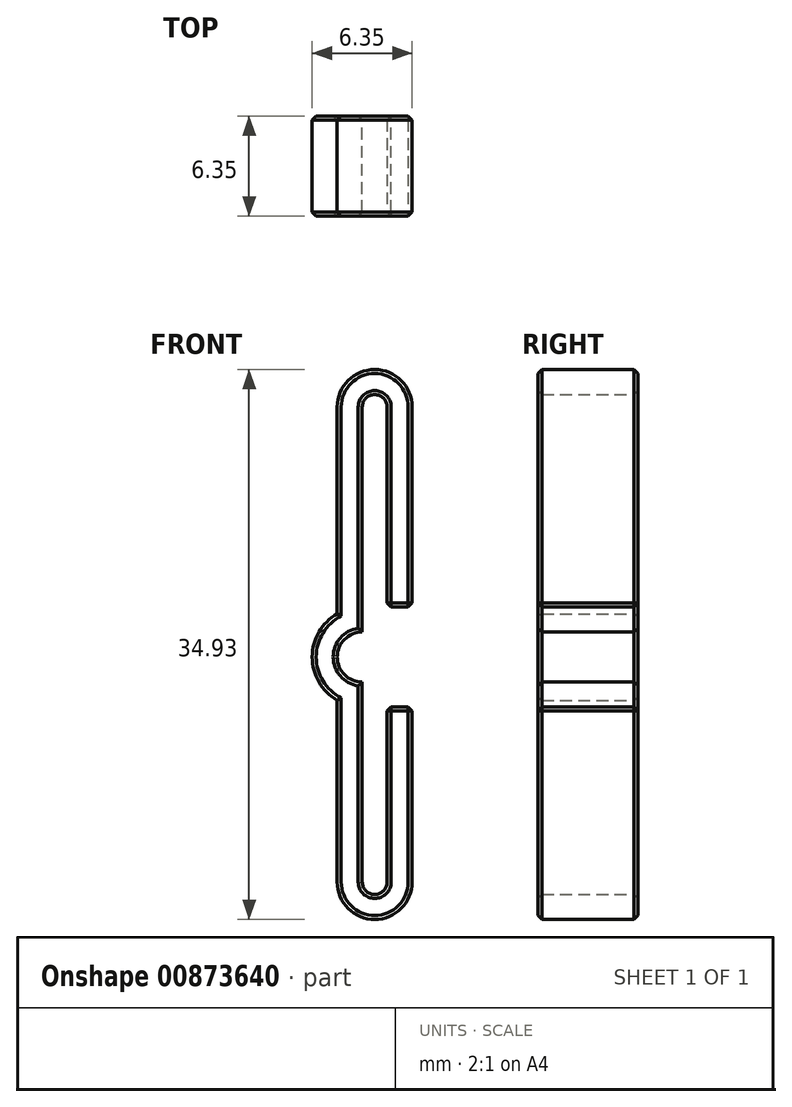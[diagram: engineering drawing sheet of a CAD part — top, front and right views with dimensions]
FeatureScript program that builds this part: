
annotation { "Feature Type Name" : "Feature", "Feature Type Description" : "" }
export const myFeature = defineFeature(function(context is Context, id is Id, definition is map)
    precondition{}
    {
        {
            var Q0;
            Q0=qCreatedBy(makeId("Front.planeOp"),FACE);
            var sketch = newSketch(context, id + "F0", { "sketchPlane" : qUnion([Q0])});
            skLineSegment(sketch, "E0", {"start": v(0, 15.88) * mm, "end": v(0, 1.59) * mm});
            skLineSegment(sketch, "E1", {"start": v(1.59, 15.88) * mm, "end": v(1.59, 3.18) * mm});
            skLineSegment(sketch, "E2", {"start": v(-1.59, 15.88) * mm, "end": v(-1.59, 2.75) * mm});
            skLineSegment(sketch, "E3", {"start": v(3.17, 15.88) * mm, "end": v(3.17, 3.18) * mm});
            skArc(sketch, "E4", {"start": v(3.17, 15.88) * mm, "mid": v(0.8, 18.26) * mm, "end": v(-1.59, 15.88) * mm});
            skArc(sketch, "E5", {"start": v(-1.59, -14.29) * mm, "mid": v(0.8, -16.67) * mm, "end": v(3.18, -14.29) * mm});
            skArc(sketch, "E6", {"start": v(0, -14.29) * mm, "mid": v(0.8, -15.08) * mm, "end": v(1.59, -14.29) * mm});
            skArc(sketch, "E7", {"start": v(1.59, 15.88) * mm, "mid": v(0.8, 16.67) * mm, "end": v(0, 15.88) * mm});
            skArc(sketch, "E8", {"start": v(0, -1.59) * mm, "mid": v(-1.59, 0) * mm, "end": v(0, 1.59) * mm});
            skArc(sketch, "E9", {"start": v(-1.59, 2.75) * mm, "mid": v(-3.18, 0) * mm, "end": v(-1.59, -2.75) * mm});
            skLineSegment(sketch, "E10.trimOffspring", {"start": v(-1.59, -2.75) * mm, "end": v(-1.59, -14.29) * mm});
            skLineSegment(sketch, "E11", {"start": v(1.59, 3.18) * mm, "end": v(3.17, 3.18) * mm});
            skLineSegment(sketch, "E12.trimOffspring", {"start": v(1.59, -3.17) * mm, "end": v(1.59, -14.29) * mm});
            skLineSegment(sketch, "E13.trimOffspring", {"start": v(3.18, -3.17) * mm, "end": v(3.18, -14.29) * mm});
            skLineSegment(sketch, "E14.trimOffspring", {"start": v(0, -1.59) * mm, "end": v(0, -14.29) * mm});
            skLineSegment(sketch, "E15", {"start": v(1.59, -3.17) * mm, "end": v(3.18, -3.17) * mm});
            skSolve(sketch);
        }
        {
            var Q0;
            Q0=makeQuery(id+"F0.imprint","IMPRINT",FACE,{"disambiguationData":[TD([[makeQuery(id+"F0.imprint","IMPRINT",EDGE,{"derivedFrom":sQuery(id+"F0.wireOp",EDGE,"E0")}),-1.0]])]});
            var Q1;
            {var subQ0=sQuery(id+"F0.wireOp",EDGE,"E8");Q1=makeQuery(id+"F0.imprint","IMPRINT",FACE,{"disambiguationData":[TD([[makeQuery(id+"F0.imprint","IMPRINT",EDGE,{"derivedFrom":subQ0}),1.0]])]});}
            var Q2;
            {var subQ1=sQuery(id+"F0.wireOp",EDGE,"E5");Q2=makeQuery(id+"F0.imprint","IMPRINT",FACE,{"disambiguationData":[TD([[makeQuery(id+"F0.imprint","IMPRINT",EDGE,{"derivedFrom":subQ1}),1.0]])]});}
            extrude(context, id + "F1", {"entities" : qUnion([Q0, Q1, Q2]), "depth" : 6.35 * mm, "offsetDistance" : 25.4 * mm});
        }
        {
            var Q0;
            Q0=makeQuery(id+"F1.opExtrude","CAP_EDGE",EDGE,{"disambiguationData":[OSD([sQuery(id+"F0.wireOp",EDGE,"E2")])],"isStart":false});
            var Q1;
            Q1=makeQuery(id+"F1.opExtrude","CAP_EDGE",EDGE,{"disambiguationData":[OSD([sQuery(id+"F0.wireOp",EDGE,"E4")])],"isStart":false});
            var Q2;
            Q2=makeQuery(id+"F1.opExtrude","CAP_EDGE",EDGE,{"disambiguationData":[OSD([sQuery(id+"F0.wireOp",EDGE,"E3")])],"isStart":false});
            var Q3;
            Q3=makeQuery(id+"F1.opExtrude","CAP_EDGE",EDGE,{"disambiguationData":[OSD([sQuery(id+"F0.wireOp",EDGE,"E9")])],"isStart":false});
            var Q4;
            Q4=makeQuery(id+"F1.opExtrude","CAP_EDGE",EDGE,{"disambiguationData":[OSD([sQuery(id+"F0.wireOp",EDGE,"E10.trimOffspring")])],"isStart":false});
            var Q5;
            Q5=makeQuery(id+"F1.opExtrude","CAP_EDGE",EDGE,{"disambiguationData":[OSD([sQuery(id+"F0.wireOp",EDGE,"E5")])],"isStart":false});
            var Q6;
            Q6=makeQuery(id+"F1.opExtrude","CAP_EDGE",EDGE,{"disambiguationData":[OSD([sQuery(id+"F0.wireOp",EDGE,"E13.trimOffspring")])],"isStart":false});
            var Q7;
            Q7=makeQuery(id+"F1.opExtrude","CAP_EDGE",EDGE,{"disambiguationData":[OSD([sQuery(id+"F0.wireOp",EDGE,"E11")])],"isStart":false});
            var Q8;
            Q8=makeQuery(id+"F1.opExtrude","CAP_EDGE",EDGE,{"disambiguationData":[OSD([sQuery(id+"F0.wireOp",EDGE,"E15")])],"isStart":false});
            var Q9;
            Q9=makeQuery(id+"F1.opExtrude","CAP_EDGE",EDGE,{"disambiguationData":[OSD([sQuery(id+"F0.wireOp",EDGE,"E14.trimOffspring")])],"isStart":false});
            var Q10;
            Q10=makeQuery(id+"F1.opExtrude","CAP_EDGE",EDGE,{"disambiguationData":[OSD([sQuery(id+"F0.wireOp",EDGE,"E8")])],"isStart":false});
            var Q11;
            Q11=makeQuery(id+"F1.opExtrude","CAP_EDGE",EDGE,{"disambiguationData":[OSD([sQuery(id+"F0.wireOp",EDGE,"E0")])],"isStart":false});
            var Q12;
            Q12=makeQuery(id+"F1.opExtrude","SWEPT_EDGE",EDGE,{"disambiguationData":[OSD([sQuery(id+"F0.wireOp",EDGE,"E1"),sQuery(id+"F0.wireOp",EDGE,"E11")])]});
            var Q13;
            Q13=makeQuery(id+"F1.opExtrude","SWEPT_EDGE",EDGE,{"disambiguationData":[OSD([sQuery(id+"F0.wireOp",EDGE,"E12.trimOffspring"),sQuery(id+"F0.wireOp",EDGE,"E15")])]});
            var Q14;
            Q14=makeQuery(id+"F1.opExtrude","CAP_EDGE",EDGE,{"disambiguationData":[OSD([sQuery(id+"F0.wireOp",EDGE,"E15")])],"isStart":true});
            var Q15;
            Q15=makeQuery(id+"F1.opExtrude","SWEPT_EDGE",EDGE,{"disambiguationData":[OSD([sQuery(id+"F0.wireOp",EDGE,"E13.trimOffspring"),sQuery(id+"F0.wireOp",EDGE,"E15")])]});
            var Q16;
            Q16=makeQuery(id+"F1.opExtrude","CAP_EDGE",EDGE,{"disambiguationData":[OSD([sQuery(id+"F0.wireOp",EDGE,"E11")])],"isStart":true});
            var Q17;
            Q17=makeQuery(id+"F1.opExtrude","SWEPT_EDGE",EDGE,{"disambiguationData":[OSD([sQuery(id+"F0.wireOp",EDGE,"E3"),sQuery(id+"F0.wireOp",EDGE,"E11")])]});
            var Q18;
            Q18=makeQuery(id+"F1.opExtrude","CAP_EDGE",EDGE,{"disambiguationData":[OSD([sQuery(id+"F0.wireOp",EDGE,"E3")])],"isStart":true});
            var Q19;
            Q19=makeQuery(id+"F1.opExtrude","CAP_EDGE",EDGE,{"disambiguationData":[OSD([sQuery(id+"F0.wireOp",EDGE,"E13.trimOffspring")])],"isStart":true});
            var Q20;
            Q20=makeQuery(id+"F1.opExtrude","CAP_EDGE",EDGE,{"disambiguationData":[OSD([sQuery(id+"F0.wireOp",EDGE,"E9")])],"isStart":true});
            var Q21;
            Q21=makeQuery(id+"F1.opExtrude","CAP_EDGE",EDGE,{"disambiguationData":[OSD([sQuery(id+"F0.wireOp",EDGE,"E12.trimOffspring")])],"isStart":true});
            var Q22;
            Q22=makeQuery(id+"F1.opExtrude","CAP_EDGE",EDGE,{"disambiguationData":[OSD([sQuery(id+"F0.wireOp",EDGE,"E1")])],"isStart":true});
            var Q23;
            Q23=makeQuery(id+"F1.opExtrude","CAP_EDGE",EDGE,{"disambiguationData":[OSD([sQuery(id+"F0.wireOp",EDGE,"KuLfTwDx-zEdX-Pjij-sEFi-Q8d45hJH9Kas")])],"isStart":true});
            var Q24;
            Q24=makeQuery(id+"F1.opExtrude","CAP_EDGE",EDGE,{"disambiguationData":[OSD([sQuery(id+"F0.wireOp",EDGE,"E8")])],"isStart":true});
            chamfer(context, id + "F2", {"entities" : qUnion([Q0, Q1, Q2, Q3, Q4, Q5, Q6, Q7, Q8, Q9, Q10, Q11, Q12, Q13, Q14, Q15, Q16, Q17, Q18, Q19, Q20, Q21, Q22, Q23, Q24]), "width" : 0.25 * mm, "tangentPropagation" : true});
        }
    });
